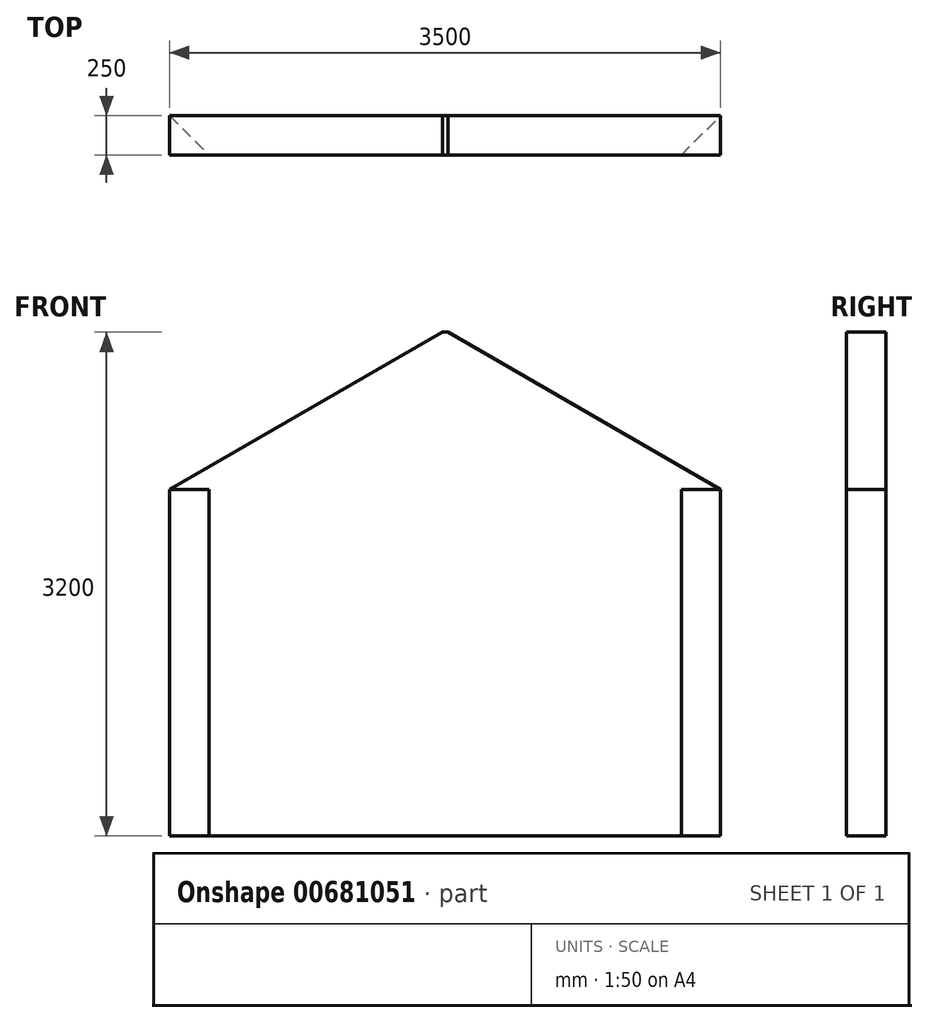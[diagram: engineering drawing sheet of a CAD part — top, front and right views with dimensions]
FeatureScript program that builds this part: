
annotation { "Feature Type Name" : "Feature", "Feature Type Description" : "" }
export const myFeature = defineFeature(function(context is Context, id is Id, definition is map)
    precondition{}
    {
        {
            var Q0;
            Q0=qCreatedBy(makeId("Front.planeOp"),FACE);
            var sketch = newSketch(context, id + "F0", { "sketchPlane" : qUnion([Q0])});
            skLineSegment(sketch, "E0.bottom", {"start": v(0, 0) * mm, "end": v(3500, 0) * mm});
            skLineSegment(sketch, "E0.top", {"start": v(0, 2200) * mm, "end": v(3500, 2200) * mm});
            skLineSegment(sketch, "E0.left", {"start": v(0, 0) * mm, "end": v(0, 2200) * mm});
            skLineSegment(sketch, "E0.right", {"start": v(3500, 0) * mm, "end": v(3500, 2200) * mm});
            skSolve(sketch);
        }
        {
            var Q0;
            Q0=qSketchRegion(id+"F0",true);
            extrude(context, id + "F1", {"entities" : qUnion([Q0]), "depth" : 250 * mm, "offsetDistance" : 25 * mm});
        }
        {
            var Q0;
            Q0=makeQuery(id+"F1.opExtrude","SWEPT_FACE",FACE,{"disambiguationData":[OSD([sQuery(id+"F0.wireOp",EDGE,"E0.top")])]});
            var sketch = newSketch(context, id + "F2", { "sketchPlane" : qUnion([Q0])});
            skLineSegment(sketch, "E1", {"start": v(0, 0) * mm, "end": v(250, -250) * mm});
            skLineSegment(sketch, "E2", {"start": v(250, -250) * mm, "end": v(0, -250) * mm});
            skLineSegment(sketch, "E3", {"start": v(0, -250) * mm, "end": v(0, 0) * mm});
            skLineSegment(sketch, "E4", {"start": v(3500, -250) * mm, "end": v(3250, -250) * mm});
            skLineSegment(sketch, "E5", {"start": v(3250, -250) * mm, "end": v(3500, 0) * mm});
            skLineSegment(sketch, "E6", {"start": v(3500, 0) * mm, "end": v(3500, -250) * mm});
            skLineSegment(sketch, "E7", {"start": v(1750, -250) * mm, "end": v(1750, 0) * mm, "construction": true});
            skSolve(sketch);
        }
        {
            var Q0;
            Q0=qSketchRegion(id+"F2",true);
            extrude(context, id + "F3", {"entities" : qUnion([Q0]), "operationType" : NewBodyOperationType.REMOVE, "endBound" : BoundingType.THROUGH_ALL, "oppositeDirection" : true, "depth" : 25 * mm, "offsetDistance" : 25 * mm});
        }
        {
            var Q0;
            Q0=makeQuery(id+"F1.opExtrude","SWEPT_FACE",FACE,{"disambiguationData":[OSD([sQuery(id+"F0.wireOp",EDGE,"E0.top")])]});
            var sketch = newSketch(context, id + "F4", { "sketchPlane" : qUnion([Q0])});
            skLineSegment(sketch, "E8.bottom", {"start": v(3500, 0) * mm, "end": v(0, 0) * mm});
            skLineSegment(sketch, "E8.top", {"start": v(3500, -250) * mm, "end": v(0, -250) * mm});
            skLineSegment(sketch, "E8.left", {"start": v(3500, 0) * mm, "end": v(3500, -250) * mm});
            skLineSegment(sketch, "E8.right", {"start": v(0, 0) * mm, "end": v(0, -250) * mm});
            skSolve(sketch);
        }
        {
            var Q0;
            Q0 = qSketchRegion(id + "F4", true);
            extrude(context, id + "F5", {"entities" : qUnion([Q0]), "operationType" : NewBodyOperationType.ADD, "depth" : 1000 * mm, "offsetDistance" : 25 * mm});
        }
        {
            var Q0;
            Q0=makeQuery(id+"F5.boolean.opBoolean","MERGE",FACE,{"derivedFrom":[makeQuery(id+"F1.opExtrude","CAP_FACE",FACE,{"disambiguationData":[OSD([sQuery(id+"F0.wireOp",EDGE,"E0.bottom"),sQuery(id+"F0.wireOp",EDGE,"E0.top"),sQuery(id+"F0.wireOp",EDGE,"E0.left"),sQuery(id+"F0.wireOp",EDGE,"E0.right")])],"isStart":false}),makeQuery(id+"F5.opExtrude","SWEPT_FACE",FACE,{"disambiguationData":[OSD([sQuery(id+"F4.wireOp",EDGE,"E8.top")])]})]});
            var sketch = newSketch(context, id + "F6", { "sketchPlane" : qUnion([Q0])});
            skLineSegment(sketch, "E9", {"start": v(0, 2200) * mm, "end": v(1750, 3210.36) * mm});
            skLineSegment(sketch, "E10", {"start": v(1750, 3210.36) * mm, "end": v(3500, 2200) * mm});
            skLineSegment(sketch, "E11", {"start": v(3500, 2200) * mm, "end": v(3500, 3200) * mm});
            skLineSegment(sketch, "E12", {"start": v(3500, 3200) * mm, "end": v(0, 3200) * mm});
            skLineSegment(sketch, "E13", {"start": v(0, 3200) * mm, "end": v(0, 2200) * mm});
            skLineSegment(sketch, "E14", {"start": v(1750, 3200) * mm, "end": v(1750, 0) * mm, "construction": true});
            skSolve(sketch);
        }
        {
            var Q0;
            Q0 = qSketchRegion(id + "F6", true);
            extrude(context, id + "F7", {"entities" : qUnion([Q0]), "operationType" : NewBodyOperationType.REMOVE, "endBound" : BoundingType.THROUGH_ALL, "oppositeDirection" : true, "depth" : 25 * mm, "offsetDistance" : 25 * mm});
        }
    });
